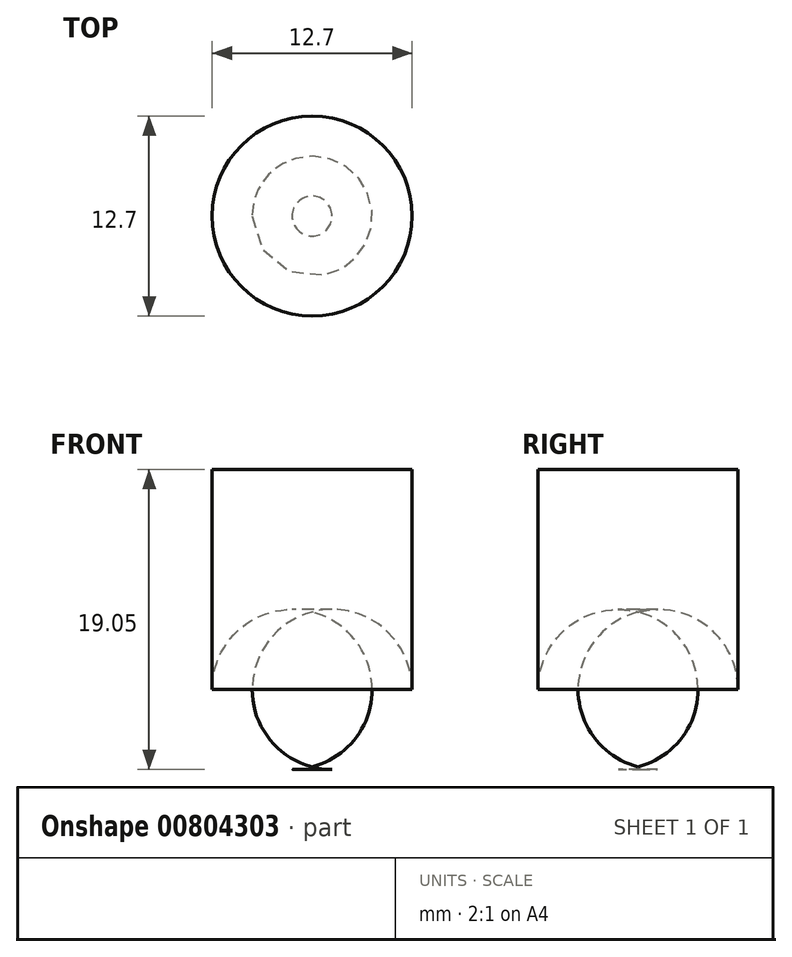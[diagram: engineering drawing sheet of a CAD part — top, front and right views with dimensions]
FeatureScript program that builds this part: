
annotation { "Feature Type Name" : "Feature", "Feature Type Description" : "" }
export const myFeature = defineFeature(function(context is Context, id is Id, definition is map)
    precondition{}
    {
        {
            var Q0;
            Q0=qCreatedBy(makeId("Top.planeOp"),FACE);
            var sketch = newSketch(context, id + "F0", { "sketchPlane" : qUnion([Q0])});
            skCircle(sketch, "E0", {"center": v(0, 0) * mm, "radius": 6.35 * mm});
            skSolve(sketch);
        }
        {
            var Q0;
            Q0=makeQuery(id+"F0.imprint","IMPRINT",FACE,{"disambiguationData":[TD([[makeQuery(id+"F0.imprint","IMPRINT",EDGE,{"derivedFrom":sQuery(id+"F0.wireOp",EDGE,"E0")}),1.0]])]});
            extrude(context, id + "F1", {"entities" : qUnion([Q0]), "depth" : 19.05 * mm, "offsetDistance" : 25.4 * mm});
        }
        {
            var Q0;
            Q0=makeQuery(id+"F1.opExtrude","CAP_FACE",FACE,{"disambiguationData":[OSD([sQuery(id+"F0.wireOp",EDGE,"E0")])],"isStart":true});
            fillet(context, id + "F2", {"entities" : qUnion([Q0]), "radius" : 5.08 * mm, "tangentPropagation" : true, "allowEdgeOverflow" : false});
        }
    });
